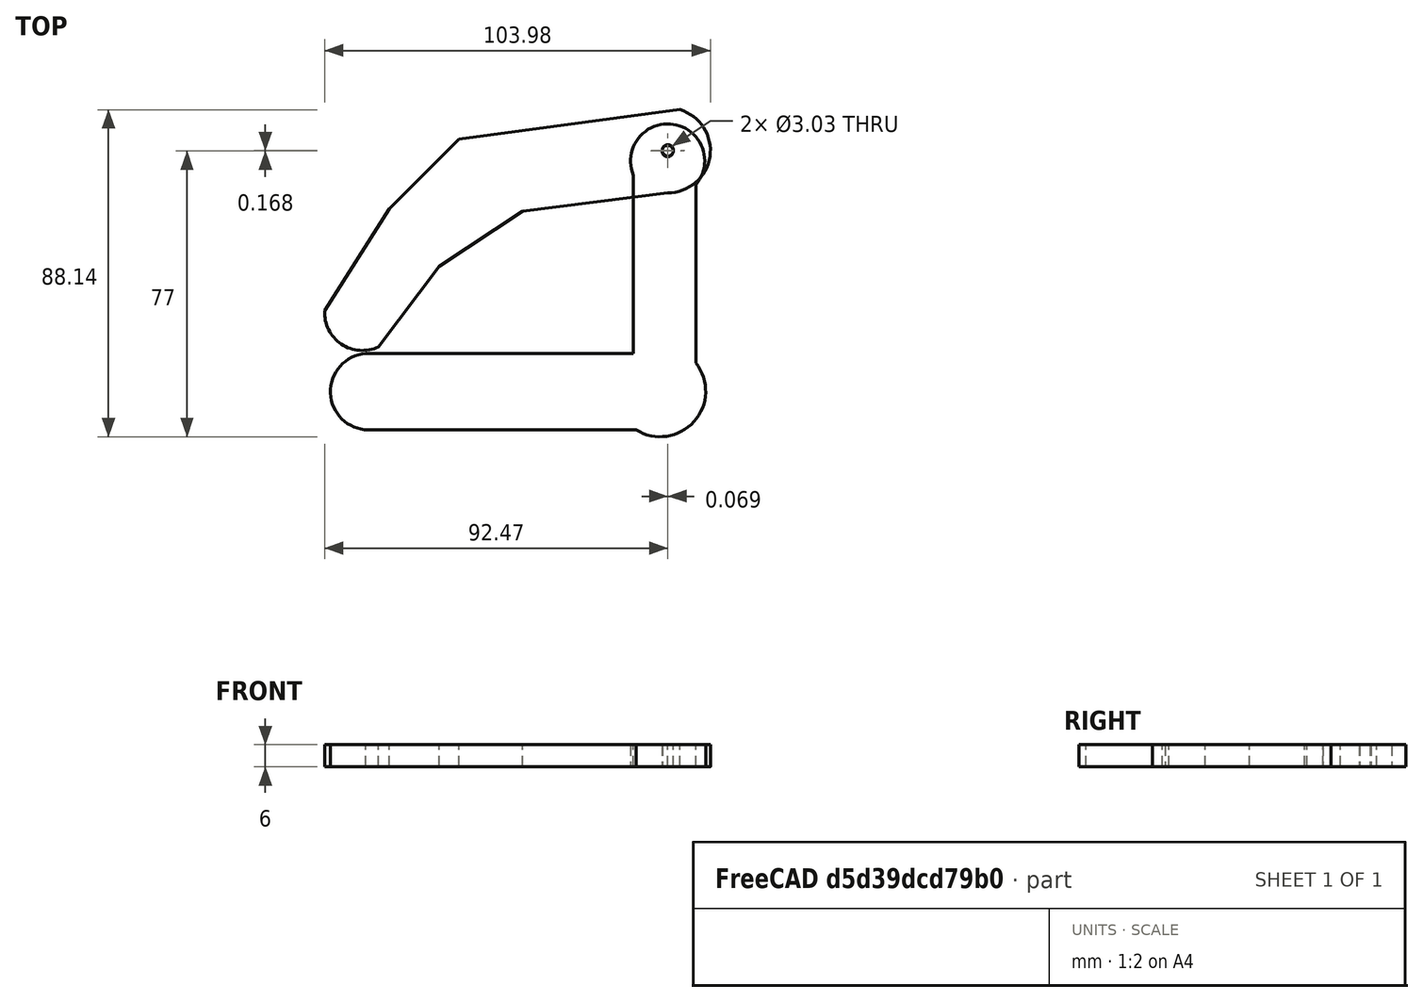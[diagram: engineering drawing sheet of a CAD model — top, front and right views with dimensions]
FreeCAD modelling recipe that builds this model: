
FCSTD DOCUMENT  (FreeCAD 1.0R38806 (Git))
Label: Pinza
License: All rights reserved
LicenseURL: https://en.wikipedia.org/wiki/All_rights_reserved
objects: Sketcher::SketchObject×2, PartDesign::Pad×2, PartDesign::Body×2, Image::ImagePlane×1
note: 12 computed .brp shape members not serialized (recipe doc carries the construction recipe); baked Part::Feature solids carry a one-line shape summary decoded from their .brp

FEATURE [Image::ImagePlane] pieza_cerrado_s  label="pieza-cerrado-s"
  Placement = pos=(-54.5,-51.5,0) rot=(0,0,1;0rad)
  XSize = 196.825
  YSize = 278.307
FEATURE [Sketcher::SketchObject] Sketch
  ArcFitTolerance = 1e-06
  AttachmentSupport = -> [XY_Plane]
  FullyConstrained = false
  MakeInternals = false
  MapMode = 5
  sketch-geometry (8):
    g0: LineSegment StartX=-81.4318 StartY=-54.5923 StartZ=0 EndX=-9.22185 EndY=-54.5923 EndZ=0
    g1: LineSegment StartX=-9.22185 StartY=-54.5923 StartZ=0 EndX=-9.22185 EndY=-6.55229 EndZ=0
    g2: ArcOfCircle CenterX=0 CenterY=-2.69041 CenterZ=0 NormalX=0 NormalY=0 NormalZ=1 AngleXU=0 Radius=9.99783 StartAngle=5.58327 EndAngle=9.82136
    g3: LineSegment StartX=7.64731 StartY=-9.13054 StartZ=0 EndX=7.64731 EndY=-57.1705 EndZ=0
    g4: LineSegment StartX=-80.7174 StartY=-75.16 StartZ=0 EndX=-8.50745 EndY=-75.16 EndZ=0
    g5: ArcOfCircle CenterX=-2.03426 CenterY=-64.7247 CenterZ=0 NormalX=0 NormalY=0 NormalZ=1 AngleXU=0 Radius=12.28 StartAngle=4.15717 EndAngle=6.94577
    g6: ArcOfCircle CenterX=-80.623 CenterY=-64.8605 CenterZ=0 NormalX=0 NormalY=0 NormalZ=1 AngleXU=0 Radius=10.3 StartAngle=1.64941 EndAngle=4.70322
    g7: Circle CenterX=0 CenterY=0 CenterZ=0 NormalX=0 NormalY=0 NormalZ=1 AngleXU=0 Radius=1.515
  constraints (21):
    c: Horizontal(g0)
    c: Coincident(g0,g1)
    c: Vertical(g1)
    c: PointOnObject(g2,g-2)
    c: Coincident(g1,g2)
    c: DistanceY(g1,g1) = 48.04
    c: DistanceX(g0,g0) = 72.21
    c: Distance(g2,g-1) = 11.91
    c: Vertical(g3)
    c: DistanceY(g3,g3) = 48.04
    c: Coincident(g2,g3)
    c: Distance(g4) = 72.21
    c: Horizontal(g4)
    c: Coincident(g4,g5)
    c: Coincident(g5,g3)
    c: Coincident(g0,g6)
    c: Coincident(g6,g4)
    c: Radius(g6) = 10.3
    c: Radius(g5) = 12.28
    c: Coincident(g7,g-1)
    c: Diameter(g7) = 3.03
FEATURE [PartDesign::Pad] Pad
  Direction = (0,0,1)
  Length = 6
  Length2 = 10
  Profile = -> Sketch
  ReferenceAxis = -> Sketch [N_Axis]
  Refine = true
  Suppressed = false
  Type = 0
FEATURE [PartDesign::Body] Body  label="Dedo-gordo"
  AllowCompound = false
  Group = -> [Sketch,Pad]
  Origin = -> Origin
  Tip = -> Pad
FEATURE [Sketcher::SketchObject] Sketch001
  ArcFitTolerance = 1e-06
  AttachmentSupport = -> [XY_Plane001]
  FullyConstrained = false
  MakeInternals = false
  MapMode = 5
  sketch-geometry (9):
    g0: LineSegment StartX=-92.4565 StartY=-43.0577 StartZ=0 EndX=-75.0092 EndY=-15.5369 EndZ=0
    g1: LineSegment StartX=-75.0092 StartY=-15.5369 StartZ=0 EndX=-56.2049 EndY=3.24913 EndZ=0
    g2: LineSegment StartX=-56.2049 StartY=3.24913 StartZ=0 EndX=3.31128 EndY=11.1417 EndZ=0
    g3: LineSegment StartX=-77.9308 StartY=-52.758 StartZ=0 EndX=-61.5847 EndY=-31.0467 EndZ=0
    g4: LineSegment StartX=-61.5847 StartY=-31.0467 StartZ=0 EndX=-39.057 EndY=-16.2524 EndZ=0
    g5: LineSegment StartX=-39.057 StartY=-16.2524 StartZ=0 EndX=0 EndY=-11.2746 EndZ=0
    g6: ArcOfCircle CenterX=-82.3423 CenterY=-43.6379 CenterZ=0 NormalX=0 NormalY=0 NormalZ=1 AngleXU=0 Radius=10.1309 StartAngle=3.08428 EndAngle=5.16292
    g7: ArcOfCircle CenterX=0.0687624 CenterY=0.16796 CenterZ=0 NormalX=0 NormalY=0 NormalZ=1 AngleXU=0 Radius=11.4428 StartAngle=4.70638 EndAngle=7.56668
    g8: Circle CenterX=0.0687624 CenterY=0.16796 CenterZ=0 NormalX=0 NormalY=0 NormalZ=1 AngleXU=0 Radius=1.515
  constraints (11):
    c: Coincident(g0,g1)
    c: Coincident(g1,g2)
    c: Coincident(g3,g4)
    c: Coincident(g4,g5)
    c: PointOnObject(g5,g-2)
    c: Coincident(g6,g3)
    c: Coincident(g6,g0)
    c: Coincident(g7,g2)
    c: Coincident(g7,g5)
    c: Diameter(g8) = 3.03
    c: Coincident(g8,g7)
FEATURE [PartDesign::Pad] Pad001
  Direction = (0,0,1)
  Length = 6
  Length2 = 10
  Profile = -> Sketch001
  ReferenceAxis = -> Sketch001 [N_Axis]
  Refine = true
  Suppressed = false
  Type = 0
FEATURE [PartDesign::Body] Body001  label="Dedo-indice"
  AllowCompound = false
  Group = -> [Sketch001,Pad001]
  Origin = -> Origin001
  Tip = -> Pad001
